# Revit family: DCST_Счетчик водяной общедомовой_ВСКМ 90
name_source: partatom
category: Арматура трубопроводов
units: mm (PartAtom-declared; Revit-internal decimal feet)

## family parameters
Всегда вертикально = Да
На основе рабочей плоскости = Нет
Общий = Нет
При загрузке вырезать с полостями = Нет
Размер круглого соединителя = Использовать диаметр
Тип детали = Вставляется

## types (4) — shared parameters
ADSK_Единица измерения = шт.
ADSK_Завод-изготовитель = Декаст
ADSK_Количество = 1
LT = ВСКМ 90
URL = https://www.decast.com
ИПД_LoRaWAN = ♦ : LoRaWAN
ИПД_ДГ2 = ♦ : импульсный выход (геркон)
ИПД_Коллектор = ♦ : импульсный выход (открытый коллектор)
ИПД_Нет = ♦ : нет
Изготовитель = Декаст

## per-type parameters (varying)
| type | ADSK_Диаметр условный | Dm | F | F1 | F2 | Fh | L1 | L2 | R | SW | h1 | h2 | r | Диаметр условного прохода | Монтажная длина | УГО_Высота | УГО_Длина | УГО_Длина линии |
| ВСКМ 90-25 | 25 мм | 30 мм | 25 мм | 42 мм | 32 мм | 14 мм | 57 мм | 22 мм | 44.65 мм | 45 мм | 24.6 мм | 26.4 мм | 22.2 мм | 25 мм | 260 мм | 142 мм | 284 мм | 57 мм |
| ВСКМ 90-32 | 32 мм | 40 мм | 25 мм | 42 мм | 32 мм | 14 мм | 63 мм | 25 мм | 44.65 мм | 55 мм | 24.6 мм | 26.4 мм | 22.2 мм | 32 мм | 260 мм | 145 мм | 290 мм | 63 мм |
| ВСКМ 90-40 | 40 мм | 45 мм | 25 мм | 50 мм | 48 мм | 20 мм | 63 мм | 25 мм | 53.9 мм | 65 мм | 34.5 мм | 45 мм | 23.5 мм | 40 мм | 300 мм | 165 мм | 330 мм | 63 мм |
| ВСКМ 90-50 | 50 мм | 60 мм | 30 мм | 50 мм | 48 мм | 20 мм | 70 мм | 32 мм | 53.9 мм | 85 мм | 34.5 мм | 45 мм | 23.5 мм | 50 мм | 300 мм | 172 мм | 344 мм | 70 мм |
